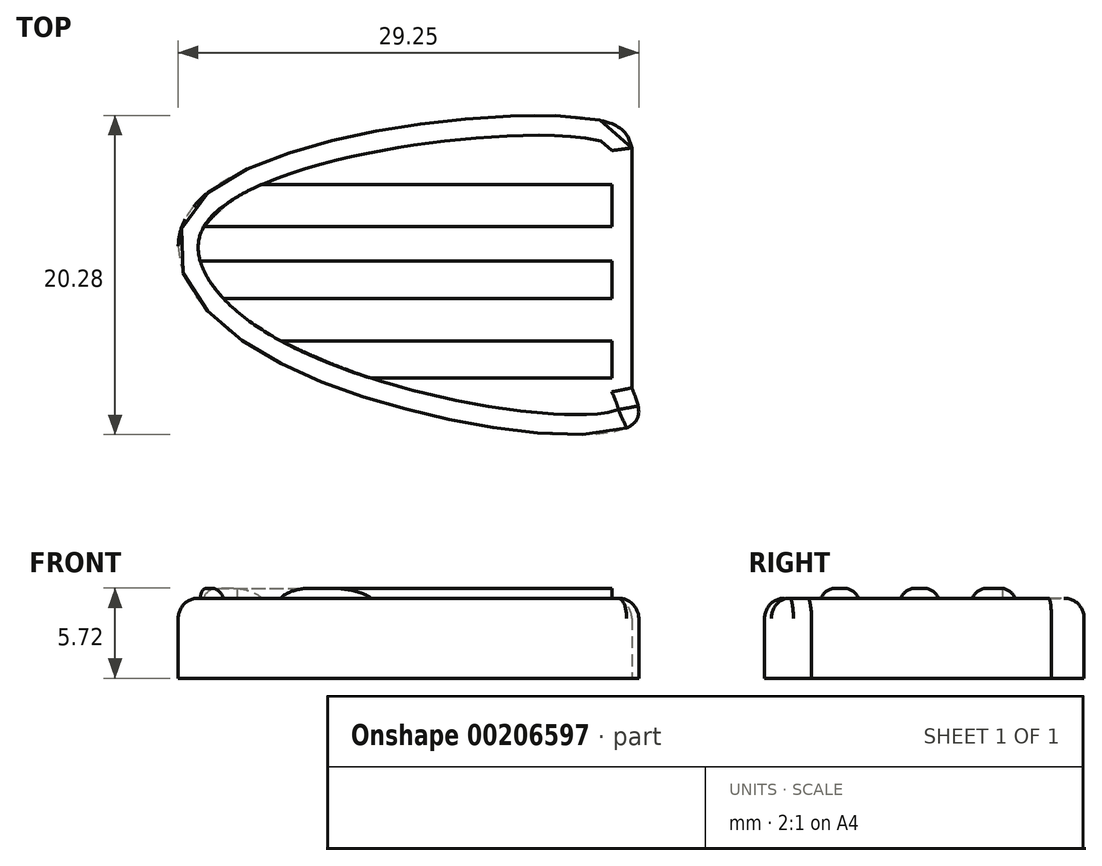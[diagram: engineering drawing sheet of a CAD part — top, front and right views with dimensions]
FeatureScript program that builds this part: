
annotation { "Feature Type Name" : "Feature", "Feature Type Description" : "" }
export const myFeature = defineFeature(function(context is Context, id is Id, definition is map)
    precondition{}
    {
        {
            var Q0;
            Q0=qCreatedBy(makeId("Top.planeOp"),FACE);
            var sketch = newSketch(context, id + "F0", { "sketchPlane" : qUnion([Q0])});
            skLineSegment(sketch, "E0", {"start": v(40.65, 7.18) * mm, "end": v(40.65, -8.06) * mm});
            skFitSpline(sketch, "E1", {"points": [v(40.65, 7.18) * mm, v(39.04, 8.83) * mm, v(13.3, 3.98) * mm, v(16.69, -5.57) * mm, v(40.65, -10.43) * mm, v(40.65, -8.06) * mm], "startDerivative": vector(-5.53, 20.53) * mm, "endDerivative": vector(-12.15, 29) * mm});
            skSolve(sketch);
        }
        {
            var Q0;
            Q0=makeQuery(id+"F0.imprint","IMPRINT",FACE,{"disambiguationData":[TD([[makeQuery(id+"F0.imprint","IMPRINT",EDGE,{"derivedFrom":sQuery(id+"F0.wireOp",EDGE,"E0")}),-1.0]])]});
            extrude(context, id + "F1", {"entities" : qUnion([Q0]), "depth" : 5.08 * mm});
        }
        {
            var Q0;
            Q0=makeQuery(id+"F1.opExtrude","CAP_EDGE",EDGE,{"disambiguationData":[OSD([sQuery(id+"F0.wireOp",EDGE,"E1")])],"isStart":false});
            var Q1;
            Q1=makeQuery(id+"F1.opExtrude","CAP_EDGE",EDGE,{"disambiguationData":[OSD([sQuery(id+"F0.wireOp",EDGE,"E0")])],"isStart":false});
            fillet(context, id + "F2", {"entities" : qUnion([Q0, Q1]), "radius" : 1.27 * mm, "tangentPropagation" : true, "allowEdgeOverflow" : false});
        }
        {
            var Q0;
            Q0=makeQuery(id+"F1.opExtrude","CAP_FACE",FACE,{"disambiguationData":[OSD([sQuery(id+"F0.wireOp",EDGE,"E0"),sQuery(id+"F0.wireOp",EDGE,"E1")])],"isStart":false});
            var sketch = newSketch(context, id + "F3", { "sketchPlane" : qUnion([Q0])});
            skLineSegment(sketch, "E2", {"start": v(39.38, 4.87) * mm, "end": v(17.17, 4.87) * mm});
            skLineSegment(sketch, "E3", {"start": v(39.38, 4.87) * mm, "end": v(39.38, 2.17) * mm});
            skLineSegment(sketch, "E4", {"start": v(39.38, 2.17) * mm, "end": v(13.47, 2.17) * mm});
            skLineSegment(sketch, "E5", {"start": v(13.24, 0) * mm, "end": v(39.38, 0) * mm});
            skLineSegment(sketch, "E6", {"start": v(39.38, 0) * mm, "end": v(39.38, -2.39) * mm});
            skLineSegment(sketch, "E7", {"start": v(39.38, -2.39) * mm, "end": v(14.72, -2.39) * mm});
            skLineSegment(sketch, "E8", {"start": v(18.36, -5.08) * mm, "end": v(39.38, -5.08) * mm});
            skLineSegment(sketch, "E9", {"start": v(39.38, -5.08) * mm, "end": v(39.38, -7.45) * mm});
            skLineSegment(sketch, "E10", {"start": v(39.38, -7.45) * mm, "end": v(24.08, -7.45) * mm});
            skArc(sketch, "E11", {"start": v(17.17, 4.87) * mm, "mid": v(15.13, 3.77) * mm, "end": v(13.47, 2.17) * mm});
            skArc(sketch, "E12", {"start": v(13.24, 0) * mm, "mid": v(13.82, -1.3) * mm, "end": v(14.72, -2.39) * mm});
            skArc(sketch, "E13", {"start": v(18.36, -5.08) * mm, "mid": v(21.18, -6.37) * mm, "end": v(24.08, -7.45) * mm});
            skSolve(sketch);
        }
        {
            var Q0;
            {var subQ5=sQuery(id+"F3.wireOp",EDGE,"E2");Q0=makeQuery(id+"F3.imprint","IMPRINT",FACE,{"disambiguationData":[TD([[makeQuery(id+"F3.imprint","IMPRINT",EDGE,{"derivedFrom":subQ5}),1.0]])]});}
            var Q1;
            {var subQ8=sQuery(id+"F3.wireOp",EDGE,"E6");Q1=makeQuery(id+"F3.imprint","IMPRINT",FACE,{"disambiguationData":[TD([[makeQuery(id+"F3.imprint","IMPRINT",EDGE,{"derivedFrom":subQ8}),1.0]])]});}
            var Q2;
            {var subQ1=sQuery(id+"F3.wireOp",EDGE,"E8");Q2=makeQuery(id+"F3.imprint","IMPRINT",FACE,{"disambiguationData":[TD([[makeQuery(id+"F3.imprint","IMPRINT",EDGE,{"derivedFrom":subQ1}),-1.0]])]});}
            extrude(context, id + "F4", {"entities" : qUnion([Q0, Q1, Q2]), "operationType" : NewBodyOperationType.ADD, "depth" : 0.64 * mm});
        }
        {
            var Q0;
            Q0=makeQuery(id+"F4.opExtrude","CAP_EDGE",EDGE,{"disambiguationData":[OSD([sQuery(id+"F3.wireOp",EDGE,"E7")])],"isStart":false});
            var Q1;
            Q1=makeQuery(id+"F4.opExtrude","CAP_EDGE",EDGE,{"disambiguationData":[OSD([sQuery(id+"F3.wireOp",EDGE,"E5")])],"isStart":false});
            var Q2;
            Q2=makeQuery(id+"F4.opExtrude","CAP_EDGE",EDGE,{"disambiguationData":[OSD([sQuery(id+"F3.wireOp",EDGE,"E8")])],"isStart":false});
            var Q3;
            Q3=makeQuery(id+"F4.opExtrude","CAP_EDGE",EDGE,{"disambiguationData":[OSD([sQuery(id+"F3.wireOp",EDGE,"E10")])],"isStart":false});
            var Q4;
            Q4=makeQuery(id+"F4.opExtrude","CAP_EDGE",EDGE,{"disambiguationData":[OSD([sQuery(id+"F3.wireOp",EDGE,"E4")])],"isStart":false});
            var Q5;
            Q5=makeQuery(id+"F4.opExtrude","CAP_EDGE",EDGE,{"disambiguationData":[OSD([sQuery(id+"F3.wireOp",EDGE,"E2")])],"isStart":false});
            fillet(context, id + "F5", {"entities" : qUnion([Q0, Q1, Q2, Q3, Q4, Q5]), "radius" : 1.02 * mm, "tangentPropagation" : true, "allowEdgeOverflow" : false});
        }
    });
